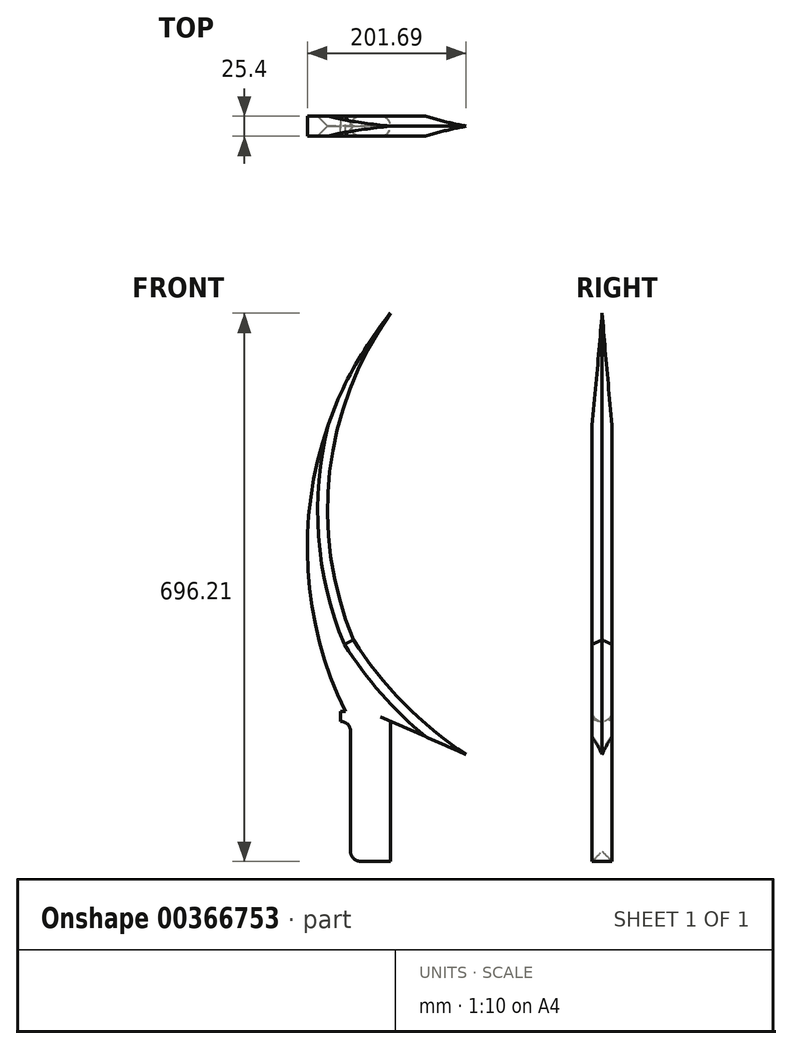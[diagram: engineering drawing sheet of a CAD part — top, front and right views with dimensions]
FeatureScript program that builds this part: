
annotation { "Feature Type Name" : "Feature", "Feature Type Description" : "" }
export const myFeature = defineFeature(function(context is Context, id is Id, definition is map)
    precondition{}
    {
        {
            var Q0;
            Q0=qCreatedBy(makeId("Front.planeOp"),FACE);
            var sketch = newSketch(context, id + "F0", { "sketchPlane" : qUnion([Q0])});
            skLineSegment(sketch, "E0", {"start": v(0, -107.42) * mm, "end": v(-25.4, -107.42) * mm});
            skLineSegment(sketch, "E1", {"start": v(-25.4, -107.42) * mm, "end": v(-25.4, 70.38) * mm});
            skLineSegment(sketch, "E2.MirrorCS", {"start": v(25.4, -107.42) * mm, "end": v(25.4, 70.38) * mm});
            skLineSegment(sketch, "E3.MirrorCS", {"start": v(0, -107.42) * mm, "end": v(25.4, -107.42) * mm});
            skLineSegment(sketch, "E4", {"start": v(-25.4, 70.38) * mm, "end": v(25.4, 70.38) * mm});
            skArc(sketch, "E5", {"start": v(25.4, 588.8) * mm, "mid": v(-77.97, 337.23) * mm, "end": v(-25.4, 70.38) * mm});
            skArc(sketch, "E6", {"start": v(25.4, 588.8) * mm, "mid": v(-50.2, 277.53) * mm, "end": v(109.72, 0) * mm});
            skLineSegment(sketch, "E7", {"start": v(-25.4, 70.38) * mm, "end": v(-38.1, 70.38) * mm});
            skLineSegment(sketch, "E8", {"start": v(-38.1, 70.38) * mm, "end": v(-38.1, 83.08) * mm});
            skLineSegment(sketch, "E9", {"start": v(-38.1, 83.08) * mm, "end": v(-31.88, 83.08) * mm});
            skLineSegment(sketch, "E10", {"start": v(25.4, 70.38) * mm, "end": v(121.47, 28.22) * mm});
            skArc(sketch, "E11", {"start": v(-21.87, 173.99) * mm, "mid": v(42.13, 93.55) * mm, "end": v(121.47, 28.22) * mm});
            skSolve(sketch);
        }
        {
            var Q0;
            Q0 = qSketchRegion(id + "F0", true);
            extrude(context, id + "F1", {"entities" : qUnion([Q0]), "depth" : 25.4 * mm});
        }
        {
            var Q0;
            Q0=makeQuery(id+"F1.opExtrude","CAP_EDGE",EDGE,{"disambiguationData":[OSD([sQuery(id+"F0.wireOp",EDGE,"E2.MirrorCS")])],"isStart":true});
            var Q1;
            Q1=makeQuery(id+"F1.opExtrude","CAP_EDGE",EDGE,{"disambiguationData":[OSD([sQuery(id+"F0.wireOp",EDGE,"E2.MirrorCS")])],"isStart":false});
            var Q2;
            Q2=makeQuery(id+"F1.opExtrude","CAP_EDGE",EDGE,{"disambiguationData":[OSD([sQuery(id+"F0.wireOp",EDGE,"E1")])],"isStart":true});
            var Q3;
            Q3=makeQuery(id+"F1.opExtrude","SWEPT_FACE",FACE,{"disambiguationData":[OSD([sQuery(id+"F0.wireOp",EDGE,"E1")])]});
            fillet(context, id + "F2", {"entities" : qUnion([Q0, Q1, Q2, Q3]), "radius" : 12.7 * mm, "tangentPropagation" : true, "allowEdgeOverflow" : false});
        }
        {
            var Q0;
            Q0=makeQuery(id+"F1.opExtrude","CAP_EDGE",EDGE,{"disambiguationData":[OSD([sQuery(id+"F0.wireOp",EDGE,"E11")])],"isStart":true});
            var Q1;
            Q1=makeQuery(id+"F1.opExtrude","CAP_EDGE",EDGE,{"disambiguationData":[OSD([sQuery(id+"F0.wireOp",EDGE,"E11")])],"isStart":false});
            var Q2;
            Q2=makeQuery(id+"F1.opExtrude","CAP_EDGE",EDGE,{"disambiguationData":[OSD([sQuery(id+"F0.wireOp",EDGE,"E6")])],"isStart":true});
            var Q3;
            Q3=makeQuery(id+"F1.opExtrude","CAP_EDGE",EDGE,{"disambiguationData":[OSD([sQuery(id+"F0.wireOp",EDGE,"E6")])],"isStart":false});
            chamfer(context, id + "F3", {"entities" : qUnion([Q0, Q1, Q2, Q3]), "chamferType" : ChamferType.OFFSET_ANGLE, "width" : 12.7 * mm, "oppositeDirection" : false, "angle" : 45 * degree, "tangentPropagation" : true});
        }
    });
